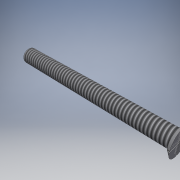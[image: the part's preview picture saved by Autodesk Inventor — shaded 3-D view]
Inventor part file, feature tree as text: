
AUTODESK INVENTOR PART (.ipt)
format: ipt  version: 2016 (Build 200138000, 138)  size: 127,488 bytes
history: native  units: in
note: dims shown in document units (in); Inventor stores cm internally (conversion verified against a paired STEP export)
features: extrude x3, sketch x3, chamfer x1, thread x1
ambient origin geometry x8: Origin, YZ Plane, XZ Plane, XY Plane, X Axis, Y Axis, Z Axis, Center Point
bodies: Solid1 (feature_tree)
feature tree (8):
  extrude  "Extrusion1"  Depth=2.5in TaperAngle=0.0deg
  extrude  "Extrusion2"  Depth=0.05in TaperAngle=0.0deg
  chamfer  "Chamfer1"  Distance=0.05in Angle=45.0deg
  extrude  "Extrusion3"  Depth=0.02in
  thread  "Thread1"  [1 undecoded]
  sketch  "Sketch1"  dims[d0=0.25in d1=2.5in d2=0.0in]
  sketch  "Sketch2"  dims[d3=0.4in d4=0.05in d5=0.0in d6=0.05in d7=0.125in d8=45.0deg]
  sketch  "Sketch3"  dims[d9=0.02in d10=0.4in d11=0.4in d12=0.02in d13=0.02in d14=0.0in d15=1.0in d16=0.0in]
note: 1 required parameter value undecoded (feature->parameter linkage not recoverable at this tier; creation-order binding heuristic only, values carry confidence <= 0.55)
